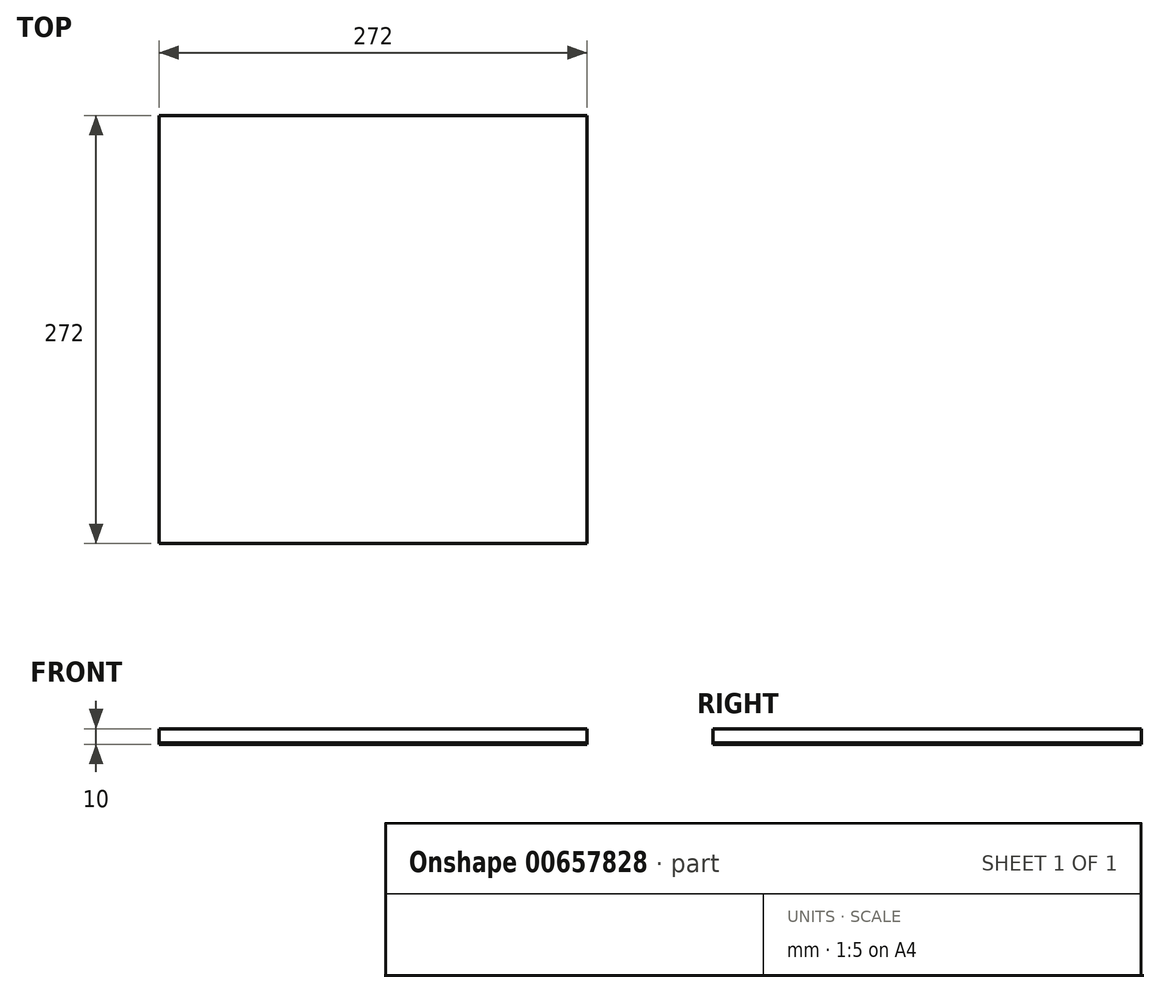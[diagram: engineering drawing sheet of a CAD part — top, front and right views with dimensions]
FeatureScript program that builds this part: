
annotation { "Feature Type Name" : "Feature", "Feature Type Description" : "" }
export const myFeature = defineFeature(function(context is Context, id is Id, definition is map)
    precondition{}
    {
        {
            var Q0;
            Q0=qCreatedBy(makeId("Top.planeOp"),FACE);
            var sketch = newSketch(context, id + "F0", { "sketchPlane" : qUnion([Q0])});
            skLineSegment(sketch, "E0.bottom", {"start": v(136, 136) * mm, "end": v(-136, 136) * mm});
            skLineSegment(sketch, "E0.top", {"start": v(136, -136) * mm, "end": v(-136, -136) * mm});
            skLineSegment(sketch, "E0.left", {"start": v(136, 136) * mm, "end": v(136, -136) * mm});
            skLineSegment(sketch, "E0.right", {"start": v(-136, 136) * mm, "end": v(-136, -136) * mm});
            skPoint(sketch, "E0.middle", {"position": v(0, 0) * mm});
            skSolve(sketch);
        }
        {
            var Q0;
            Q0 = qSketchRegion(id + "F0", true);
            extrude(context, id + "F1", {"entities" : qUnion([Q0]), "depth" : 10 * mm, "offsetDistance" : 25 * mm});
        }
        {
            var Q0;
            Q0=makeQuery(id+"F1.opExtrude","CAP_FACE",FACE,{"disambiguationData":[OSD([sQuery(id+"F0.wireOp",EDGE,"E0.bottom"),sQuery(id+"F0.wireOp",EDGE,"E0.top"),sQuery(id+"F0.wireOp",EDGE,"E0.left"),sQuery(id+"F0.wireOp",EDGE,"E0.right")])],"isStart":true});
            extrude(context, id + "F2", {"entities" : qUnion([Q0]), "depth" : 1 * mm, "offsetDistance" : 25 * mm});
        }
        {
            var Q0;
            Q0=makeQuery(id+"F1.opExtrude","CAP_FACE",FACE,{"disambiguationData":[OSD([sQuery(id+"F0.wireOp",EDGE,"E0.bottom"),sQuery(id+"F0.wireOp",EDGE,"E0.top"),sQuery(id+"F0.wireOp",EDGE,"E0.left"),sQuery(id+"F0.wireOp",EDGE,"E0.right")])],"isStart":false});
            extrude(context, id + "F3", {"entities" : qUnion([Q0]), "operationType" : NewBodyOperationType.REMOVE, "oppositeDirection" : true, "depth" : 1 * mm, "offsetDistance" : 25 * mm});
        }
    });
